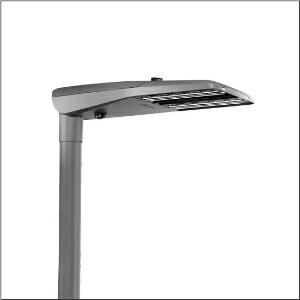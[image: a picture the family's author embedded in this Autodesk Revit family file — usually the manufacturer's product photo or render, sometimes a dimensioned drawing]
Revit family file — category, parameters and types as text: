
# Revit family: streetlight_sl_11_iq_midi___st0_5a_5xc3b51y08me_9d3e
name_source: partatom
category: Lighting Fixtures
units: mm (PartAtom-declared; Revit-internal decimal feet)

## family parameters
Cut with Voids When Loaded = No
Host = Face
Light Source = No
Part Type = Normal
Room Calculation Point = No
Round Connector Dimension = Use Diameter
Shared = No

## types (1)
- --- (1 x LED, 17940 lm, 122.7 W, 3000K)
    Apparent Load = 123 VA
    CIE Flux Codes = 43 74 97 100 100
    Color Rendering = 70
    Color Temperature = 3000K
    Default Elevation = 1800 mm
    Description = Streetlight SL 11 iQ midi, mast luminaire, primary light control with 3 zone facetted reflector, of plastic, silver coated, highly specular, primary optical cover: cover, of PMMA, transparent, light distribution: ST0.5a, light emission: direct distribution, primary light characteristic: asymmetric, installation type: post-top, side-entry, LED, High Power LED, rated luminous flux: 17.940lm, luminous efficacy: 146lm/W, light colour: 730, colour temperature: 3000K, control: presetting dimming logarithmic, Street-Remote, Auto-Match, Temp-Guard, Lumen-Switch, Night-Set, Smart-Wire, Light-Fading, Desk-Remote (wireless, voltage-free reading and setting of iQ features in the workshop via application-optimized NFC function/RFID function), optimised constant luminous flux control (CLO 2.0), with cable H07RN-F 5x 1.5mm², mains connection: 230..240V, AC, 50/60Hz, connection cable pre-assembled, cable length: 12,5m, start of lifetime: 123W, end of service life: 130W, reduction: 56W, luminaire housing, of diecast aluminium, powder-coated, Siteco® metallic grey (DB 702S), please order mast flange separately, inclination adjustable without tools: 0°, 5°, 10°, 15° (post-top) | 0°, -5°, -10°, -15° (side-entry), sealing non-destructively replaceable, multi-level sealing system, length: 780mm, width: 376mm, height: 118mm, mast flange for spigot size: 42mm (side-entry): 5XC10008XM4, 60/48mm (side-entry/post-top): 5XC10108XM2, 76/60mm (side-entry/post-top): 5XC10108XM1, equipment: Power, Smart Interface below and above, protection rating (complete): IP66, insulation class (complete): insulation class II (safety insulation), certification: CE, ENEC, VDE, UKCA, impact resistance: IK09, permissible operating ambient temperature for outdoor applications: -25..+50°C, standard-compliant lighting for roads and squares, Environmental Product Declaration (EPD) tested and certified by an independent institute, packaging unit: 1 piece

Light Distribution: ST0.5a
    Height = 118 mm
    Lamp = 1 x LED
    Lamp Light Flux = 17940 lm
    Lamp Power = 122.7 W
    Lamp count = 1
    Length = 780 mm
    Luminous efficacy = 146 lm/W
    Manufacturer = Siteco
    ModVariant = No
    Model = 5XC3B51Y08ME
    Number of Poles = 1
    OnlyDefault = Yes
    Power Factor = 1
    Product Name = Streetlight SL 11 iQ midi | ST0.5a
    Product group = mast luminaire | pylon top
    ProductGroupID = 6100
    Protection Class = Protection class II
    Protection Degree = IP 66
    RLX_Detail_Level = 1
    RLX_Emergency_Light_Flux = 0 lm
    RLX_Emergency_Type = 0
    RLX_Emergency_Type_DB = No
    RlxData = <blob elided: 74401 chars, md5=96d030e4>
    Socket = socket
    Standby Power = 0 W
    System Light Flux = 17940 lm
    System Power = 123 W
    Type Comments = factory setting: luminous flux: 100 % | dim-lin: 254 | 553 mA
    Type Image = l_1004429.jpg
    URL = http://relux.com
    VarID = @adj_082225
    Voltage = 0 V
    Weight = 0.00 kg
    Width = 376 mm

## geometry (parser evidence)
native form markers: Blend x4, Sweep x10
no freeform markers — native parametric forms only
